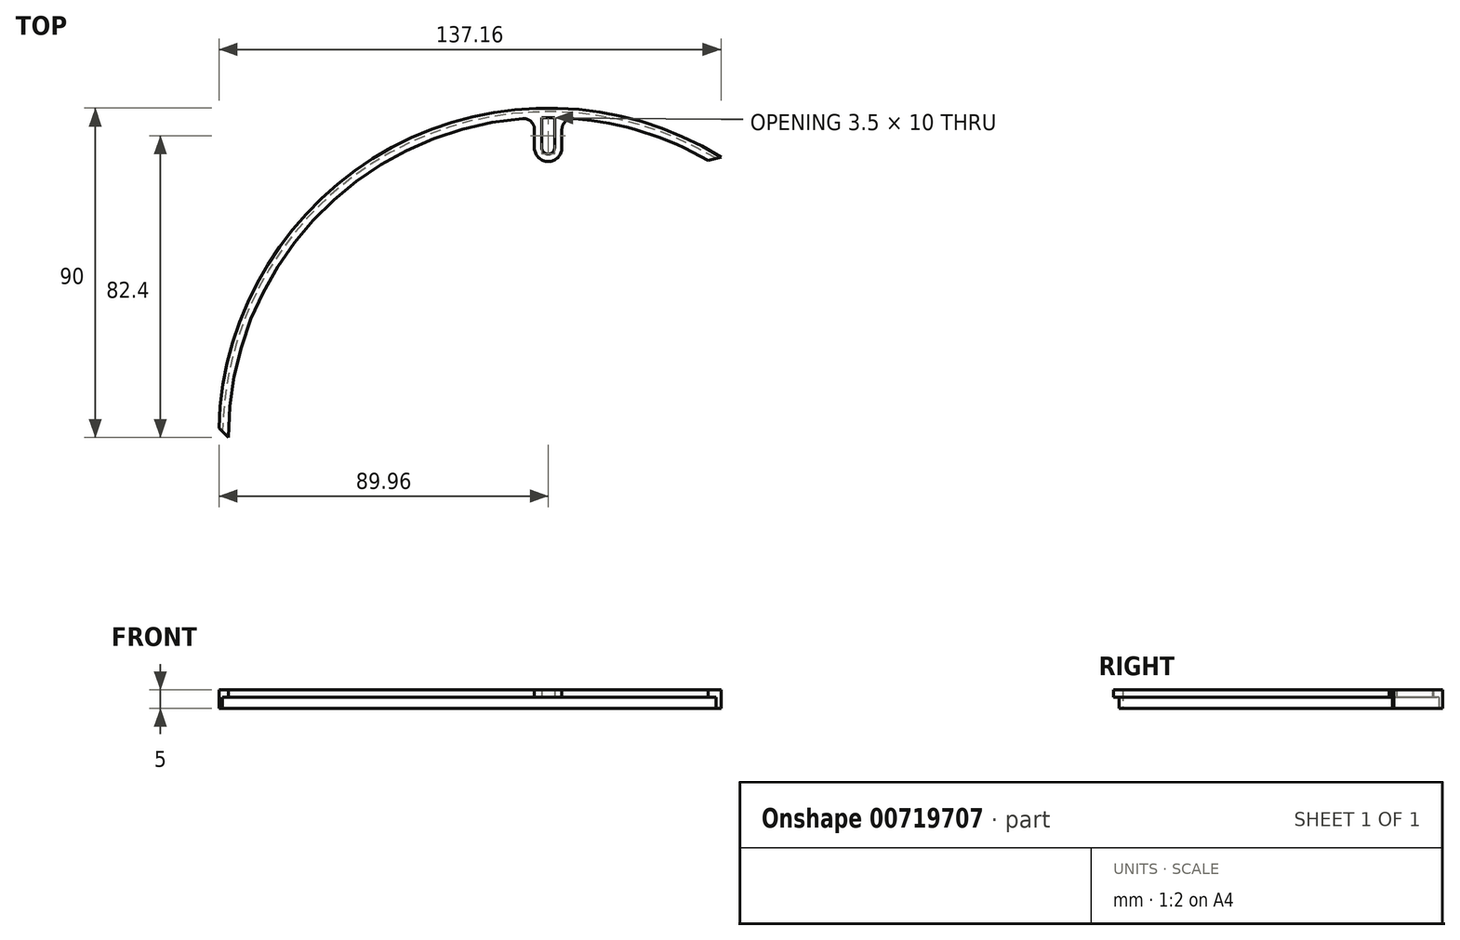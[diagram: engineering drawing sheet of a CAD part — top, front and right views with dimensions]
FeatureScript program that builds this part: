
annotation { "Feature Type Name" : "Feature", "Feature Type Description" : "" }
export const myFeature = defineFeature(function(context is Context, id is Id, definition is map)
    precondition{}
    {
        {
            var Q0;
            Q0=qCreatedBy(makeId("Top.planeOp"),FACE);
            var sketch = newSketch(context, id + "F0", { "sketchPlane" : qUnion([Q0])});
            skArc(sketch, "E0", {"start": v(47.2, 76.63) * mm, "mid": v(-42.76, 79.2) * mm, "end": v(-89.96, 2.56) * mm});
            skArc(sketch, "E1", {"start": v(-6.99, 87.12) * mm, "mid": v(-64.22, 59.28) * mm, "end": v(-87.4, 0) * mm});
            skLineSegment(sketch, "E2.right", {"start": v(-3.75, 84.13) * mm, "end": v(-3.75, 79.15) * mm});
            skArc(sketch, "E3", {"start": v(-3.75, 79.15) * mm, "mid": v(0, 75.4) * mm, "end": v(3.75, 79.15) * mm});
            skLineSegment(sketch, "E4.trimOffspring", {"start": v(3.75, 84.13) * mm, "end": v(3.75, 79.15) * mm});
            skArc(sketch, "E5.trimOffspring", {"start": v(43.7, 75.7) * mm, "mid": v(25.98, 83.45) * mm, "end": v(6.99, 87.12) * mm});
            skArc(sketch, "E6", {"start": v(-1.75, 79.15) * mm, "mid": v(0, 77.4) * mm, "end": v(1.75, 79.15) * mm});
            skLineSegment(sketch, "E7", {"start": v(-1.75, 79.15) * mm, "end": v(-1.75, 87.4) * mm});
            skLineSegment(sketch, "E8", {"start": v(-1.75, 87.4) * mm, "end": v(1.75, 87.4) * mm});
            skLineSegment(sketch, "E9", {"start": v(1.75, 87.4) * mm, "end": v(1.75, 79.15) * mm});
            skPoint(sketch, "E10.visualSharp", {"position": v(-3.75, 87.32) * mm});
            skArc(sketch, "E10.filletArc", {"start": v(-3.75, 84.13) * mm, "mid": v(-4.72, 86.33) * mm, "end": v(-6.99, 87.12) * mm});
            skPoint(sketch, "E11.visualSharp", {"position": v(3.75, 87.32) * mm});
            skArc(sketch, "E11.filletArc", {"start": v(6.99, 87.12) * mm, "mid": v(4.72, 86.33) * mm, "end": v(3.75, 84.13) * mm});
            skLineSegment(sketch, "E12", {"start": v(-87.4, 0) * mm, "end": v(-89.96, 2.56) * mm});
            skLineSegment(sketch, "E13", {"start": v(43.7, 75.7) * mm, "end": v(47.2, 76.63) * mm});
            skLineSegment(sketch, "E14", {"start": v(0, 0) * mm, "end": v(67.14, 116.28) * mm, "construction": true});
            skSolve(sketch);
        }
        {
            var Q0;
            Q0=qSketchRegion(id+"F0",true);
            extrude(context, id + "F1", {"entities" : qUnion([Q0]), "depth" : 5 * mm, "offsetDistance" : 25 * mm});
        }
        {
            var Q0;
            Q0=qCreatedBy(makeId("Top.planeOp"),FACE);
            var sketch = newSketch(context, id + "F2", { "sketchPlane" : qUnion([Q0])});
            skCircle(sketch, "E15", {"center": v(0, 0) * mm, "radius": 89 * mm});
            skSolve(sketch);
        }
        {
            var Q0;
            Q0=qSketchRegion(id+"F2",true);
            extrude(context, id + "F3", {"entities" : qUnion([Q0]), "operationType" : NewBodyOperationType.REMOVE, "depth" : 3 * mm, "offsetDistance" : 25 * mm});
        }
    });
